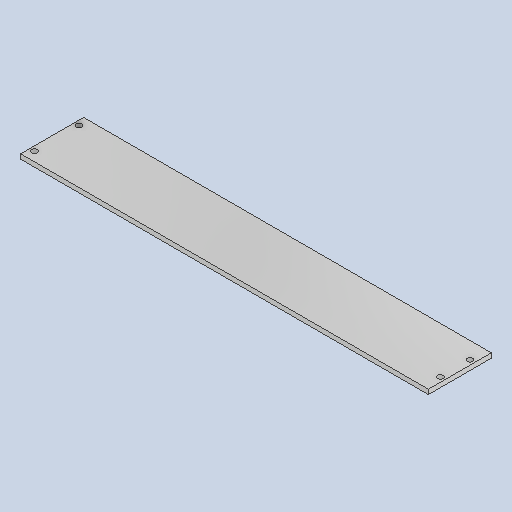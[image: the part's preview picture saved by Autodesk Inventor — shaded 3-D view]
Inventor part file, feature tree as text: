
AUTODESK INVENTOR PART (.ipt)
format: ipt  version: 2025.1 (Build 291241020, 241B)  size: 108,544 bytes
history: native  units: in
note: dims shown in document units (in); Inventor stores cm internally (conversion verified against a paired STEP export)
features: sketch x2, extrude x1, hole x1, projected_geometry x1
ambient origin geometry x8: Origin, YZ Plane, XZ Plane, XY Plane, X Axis, Y Axis, Z Axis, Center Point
bodies: Solid1 (feature_tree)
feature tree (5):
  sketch  "Sketch10"  dims[d48=11.0in d49=1.7in]
  extrude  "Extrusion8"  Depth=1.7in
  hole  "Hole2"  [1 undecoded]
  sketch  "Sketch11"  dims[d51=5.5in d52=0.125in d53=0.0in d54=0.45in d55=0.125in d56=0.45in d57=0.125in d58=0.125in d59=0.125in d60=0.25in d61=0.25in d62=0.15in d63=0.75in d64=0.375in d65=0.25in d66=0.5635in d67=1.0in d68=0.8108in]
  projected_geometry  "Projected Loop2"
note: 1 required parameter value undecoded (feature->parameter linkage not recoverable at this tier; creation-order binding heuristic only, values carry confidence <= 0.55)
